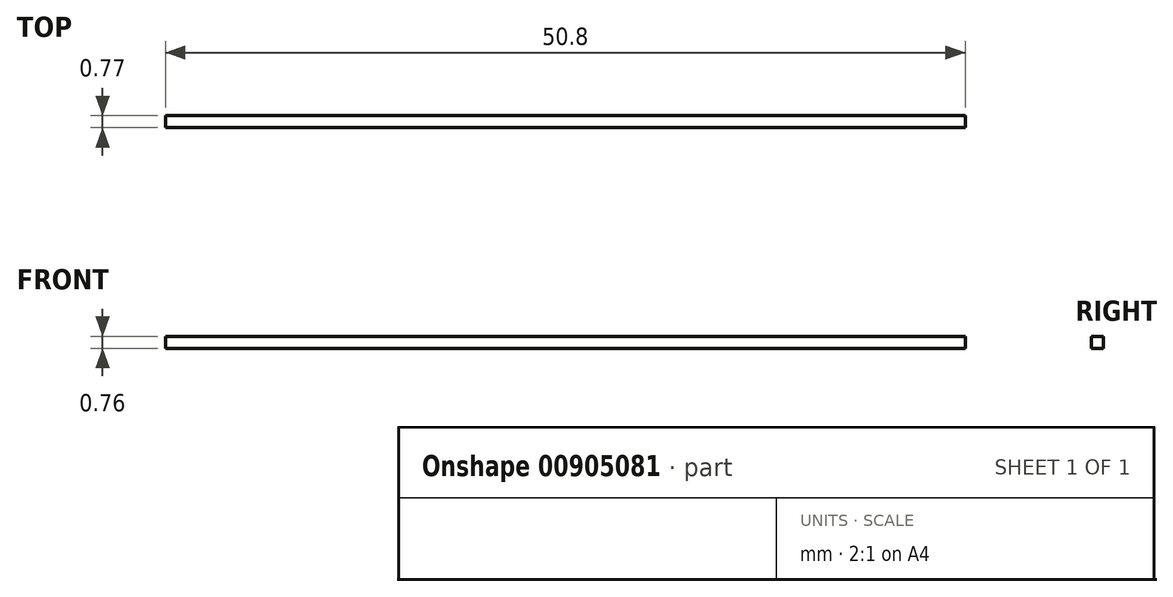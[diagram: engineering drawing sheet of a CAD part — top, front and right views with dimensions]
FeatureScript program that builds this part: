
annotation { "Feature Type Name" : "Feature", "Feature Type Description" : "" }
export const myFeature = defineFeature(function(context is Context, id is Id, definition is map)
    precondition{}
    {
        {
            var Q0;
            Q0=qCreatedBy(makeId("Top.planeOp"),FACE);
            var sketch = newSketch(context, id + "F0", { "sketchPlane" : qUnion([Q0])});
            skLineSegment(sketch, "E0.bottom", {"start": v(-21.31, 20.8) * mm, "end": v(29.49, 20.8) * mm});
            skLineSegment(sketch, "E0.top", {"start": v(-21.31, 20.03) * mm, "end": v(29.49, 20.03) * mm});
            skLineSegment(sketch, "E0.left", {"start": v(-21.31, 20.8) * mm, "end": v(-21.31, 20.03) * mm});
            skLineSegment(sketch, "E0.right", {"start": v(29.49, 20.8) * mm, "end": v(29.49, 20.03) * mm});
            skSolve(sketch);
        }
        {
            var Q0;
            Q0 = qSketchRegion(id + "F0", true);
            extrude(context, id + "F1", {"entities" : qUnion([Q0]), "depth" : 0.76 * mm, "offsetDistance" : 25.4 * mm});
        }
    });
